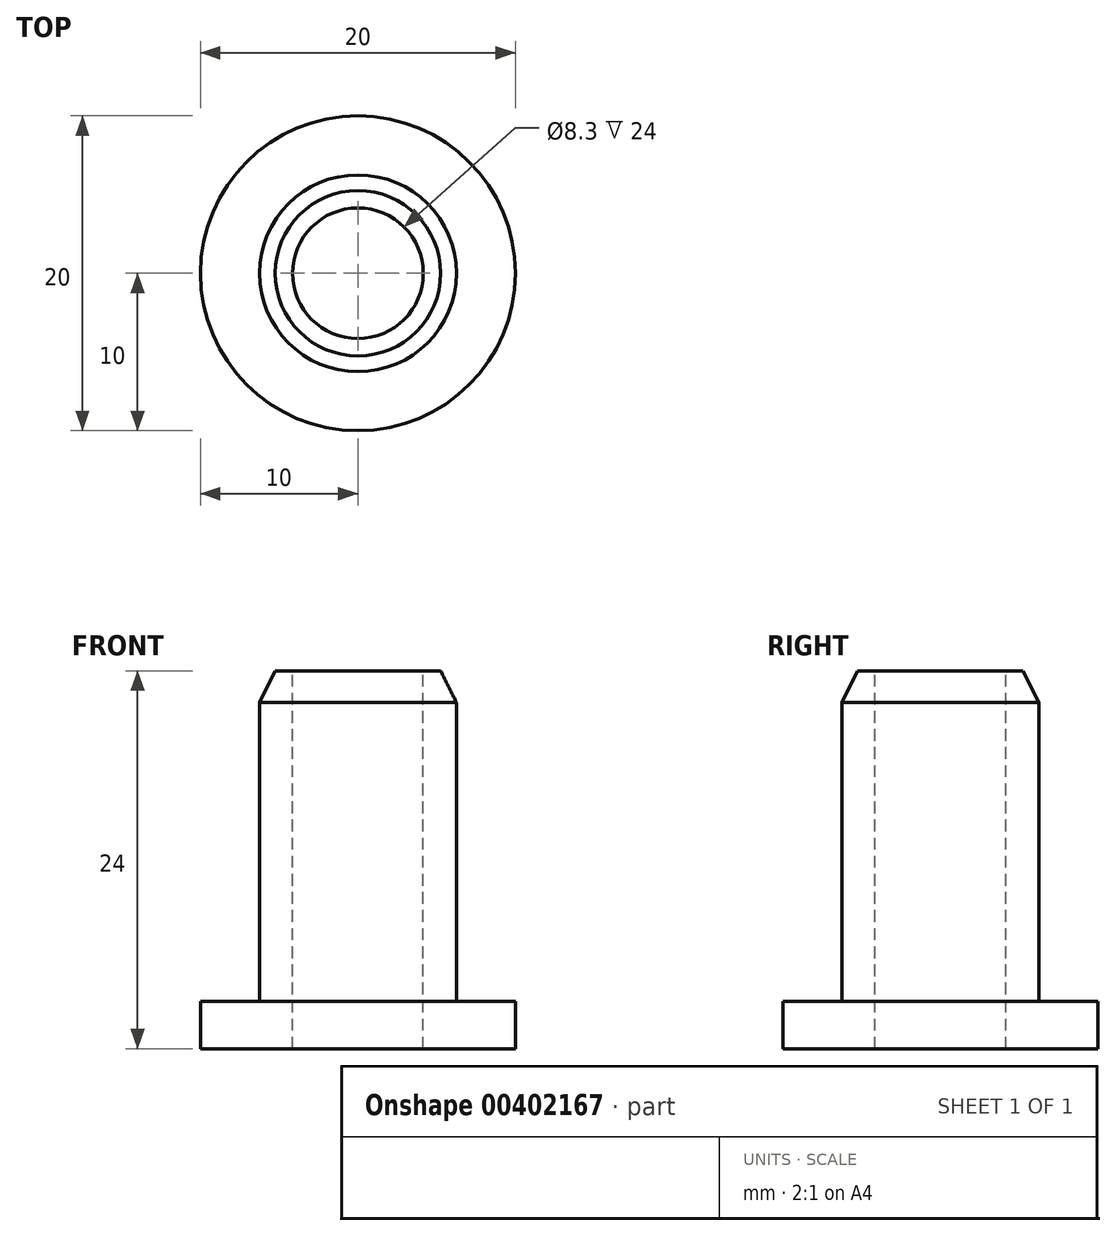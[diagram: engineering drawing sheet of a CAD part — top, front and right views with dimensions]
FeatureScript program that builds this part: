
annotation { "Feature Type Name" : "Feature", "Feature Type Description" : "" }
export const myFeature = defineFeature(function(context is Context, id is Id, definition is map)
    precondition{}
    {
        {
            var Q0;
            Q0=qCreatedBy(makeId("Top.planeOp"),FACE);
            var sketch = newSketch(context, id + "F0", { "sketchPlane" : qUnion([Q0])});
            skCircle(sketch, "E0", {"center": v(0, 0) * mm, "radius": 10 * mm});
            skSolve(sketch);
        }
        {
            var Q0;
            Q0=makeQuery(id+"F0.imprint","IMPRINT",FACE,{"disambiguationData":[TD([[makeQuery(id+"F0.imprint","IMPRINT",EDGE,{"derivedFrom":sQuery(id+"F0.wireOp",EDGE,"E0")}),1.0]])]});
            extrude(context, id + "F1", {"entities" : qUnion([Q0]), "depth" : 3 * mm});
        }
        {
            var Q0;
            Q0=makeQuery(id+"F1.opExtrude","CAP_FACE",FACE,{"disambiguationData":[OSD([sQuery(id+"F0.wireOp",EDGE,"E0")])],"isStart":false});
            var sketch = newSketch(context, id + "F2", { "sketchPlane" : qUnion([Q0])});
            skCircle(sketch, "E1", {"center": v(0, 0) * mm, "radius": 6.25 * mm});
            skSolve(sketch);
        }
        {
            var Q0;
            Q0=makeQuery(id+"F2.imprint","IMPRINT",FACE,{"disambiguationData":[TD([[makeQuery(id+"F2.imprint","IMPRINT",EDGE,{"derivedFrom":sQuery(id+"F2.wireOp",EDGE,"E1")}),1.0]])]});
            extrude(context, id + "F3", {"entities" : qUnion([Q0]), "operationType" : NewBodyOperationType.ADD, "depth" : 21 * mm});
        }
        {
            var Q0;
            Q0=makeQuery(id+"F3.opExtrude","CAP_FACE",FACE,{"disambiguationData":[OSD([sQuery(id+"F2.wireOp",EDGE,"E1")])],"isStart":false});
            var sketch = newSketch(context, id + "F4", { "sketchPlane" : qUnion([Q0])});
            skCircle(sketch, "E2", {"center": v(0, 0) * mm, "radius": 4.15 * mm});
            skSolve(sketch);
        }
        {
            var Q0;
            Q0=makeQuery(id+"F4.imprint","IMPRINT",FACE,{"disambiguationData":[TD([[makeQuery(id+"F4.imprint","IMPRINT",EDGE,{"derivedFrom":sQuery(id+"F4.wireOp",EDGE,"E2")}),1.0]])]});
            extrude(context, id + "F5", {"entities" : qUnion([Q0]), "operationType" : NewBodyOperationType.REMOVE, "oppositeDirection" : true, "depth" : 25 * mm});
        }
        {
            var Q0;
            Q0=makeQuery(id+"F3.opExtrude","CAP_EDGE",EDGE,{"disambiguationData":[OSD([sQuery(id+"F2.wireOp",EDGE,"E1")])],"isStart":false});
            chamfer(context, id + "F6", {"entities" : qUnion([Q0]), "chamferType" : ChamferType.TWO_OFFSETS, "width1" : 1 * mm, "oppositeDirection" : false, "width2" : 2 * mm, "tangentPropagation" : true});
        }
    });
